# Revit family: OASIS SHFW-WX-6235
name_source: partatom
category: Plumbing Fixtures
revit_build: Autodesk Revit 2017 (Build: 20171027_0315(x64)
units: mm (PartAtom-declared; Revit-internal decimal feet)

## family parameters
Always vertical = Yes
Cut with Voids When Loaded = No
OmniClass Number = 23.45.05.14.17.11
OmniClass Title = Shower Compartments
Part Type = Normal
Room Calculation Point = No
Round Connector Dimension = Use Diameter
Shared = No
Work Plane-Based = No

## types (6) — shared parameters
BIM Model By = www.epoch-design.com
Color = <By Category>
Grab Bar Finish = <By Category>
Manufacturer = OASIS
Sanitary Connector = Sanitary Connection
Seat Finish = <By Category>
Stainless steel = <By Category>
Type Comments = SHOWER
URL = www.oasisbath.com

## per-type parameters (varying)
| type | Bar_Horz_Back_36" | Bar_Horz_Back_48" | Bar_Horz_Left | Bar_Horz_Right | Bar_Vert | Model | Seat_Fold | Shower Rod |
| Base Model, 3SF, 3SM, FH, TLRF, TDRFDS, & TLVRF packages | No | No | No | No | No | SHFW-WX-6235/(3SF,3SM,FH,TLRF,TLRFDS,TLVRF) | No | No |
| 2BAR package | Yes | No | Yes | No | No | SHFW-WX-6235/2BAR | No | No |
| ADA-RI package | No | Yes | Yes | Yes | No | SHFW-WX-6235/ADA-RI | No | Yes |
| ADA-TL package | Yes | No | Yes | No | No | SHFW-WX-6235/ADA-TL | Yes | Yes |
| 3BAR package | Yes | No | Yes | No | Yes | SHFW-WX-6235/3BAR | No | No |
| ANS17 package | Yes | No | Yes | No | Yes | SHFW-WX-6235/ADA-TL | Yes | Yes |

## geometry (parser evidence)
native form markers: Blend x4, Sweep x12
no freeform markers — native parametric forms only
